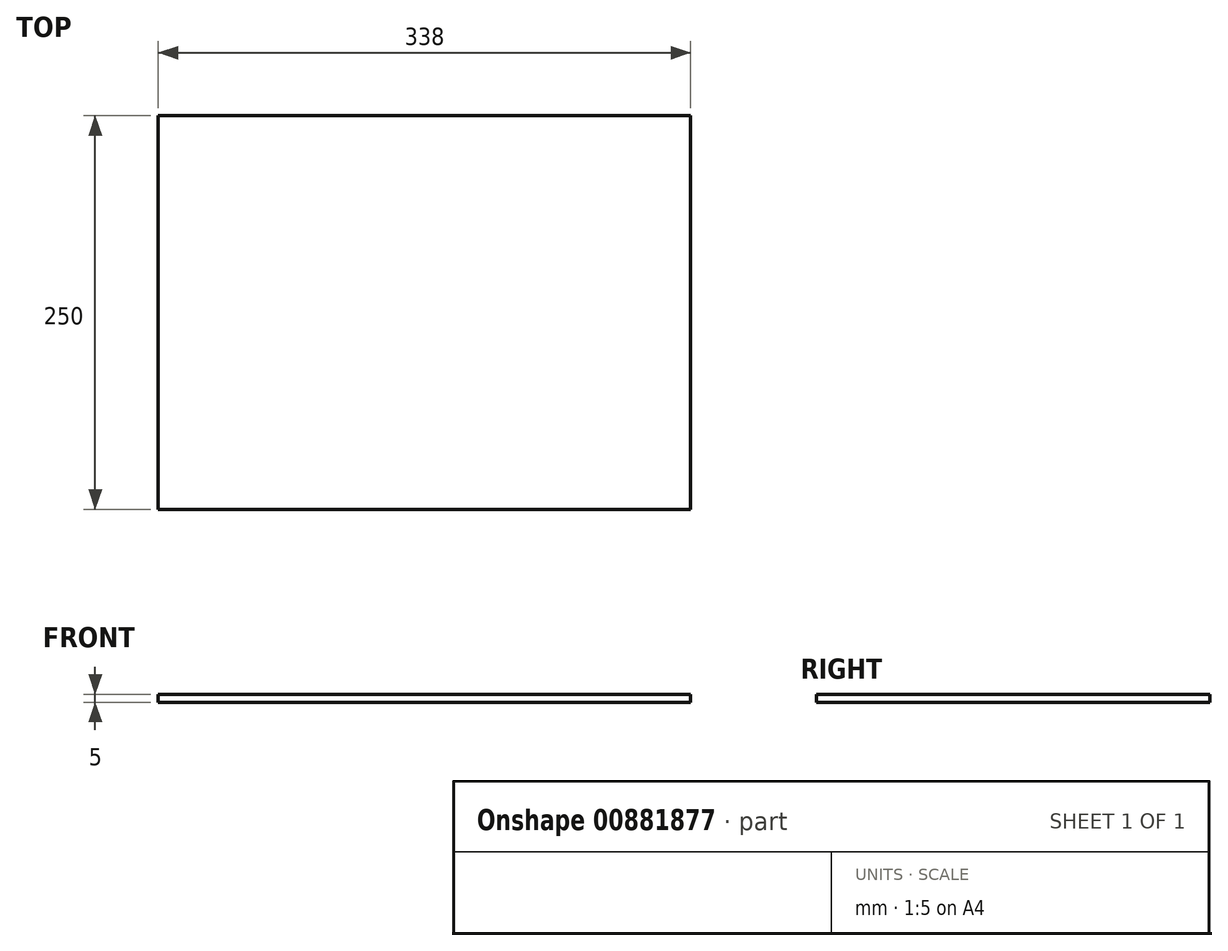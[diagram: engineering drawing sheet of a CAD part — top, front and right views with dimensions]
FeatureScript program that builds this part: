
annotation { "Feature Type Name" : "Feature", "Feature Type Description" : "" }
export const myFeature = defineFeature(function(context is Context, id is Id, definition is map)
    precondition{}
    {
        {
            var Q0;
            Q0=qCreatedBy(makeId("Top.planeOp"),FACE);
            var sketch = newSketch(context, id + "F0", { "sketchPlane" : qUnion([Q0])});
            skLineSegment(sketch, "E0.bottom", {"start": v(169, -125) * mm, "end": v(-169, -125) * mm});
            skLineSegment(sketch, "E0.top", {"start": v(169, 125) * mm, "end": v(-169, 125) * mm});
            skLineSegment(sketch, "E0.left", {"start": v(169, -125) * mm, "end": v(169, 125) * mm});
            skLineSegment(sketch, "E0.right", {"start": v(-169, -125) * mm, "end": v(-169, 125) * mm});
            skPoint(sketch, "E0.middle", {"position": v(0, 0) * mm});
            skSolve(sketch);
        }
        {
            var Q0;
            Q0 = qSketchRegion(id + "F0", true);
            extrude(context, id + "F1", {"entities" : qUnion([Q0]), "depth" : 5 * mm, "offsetDistance" : 25 * mm});
        }
    });
